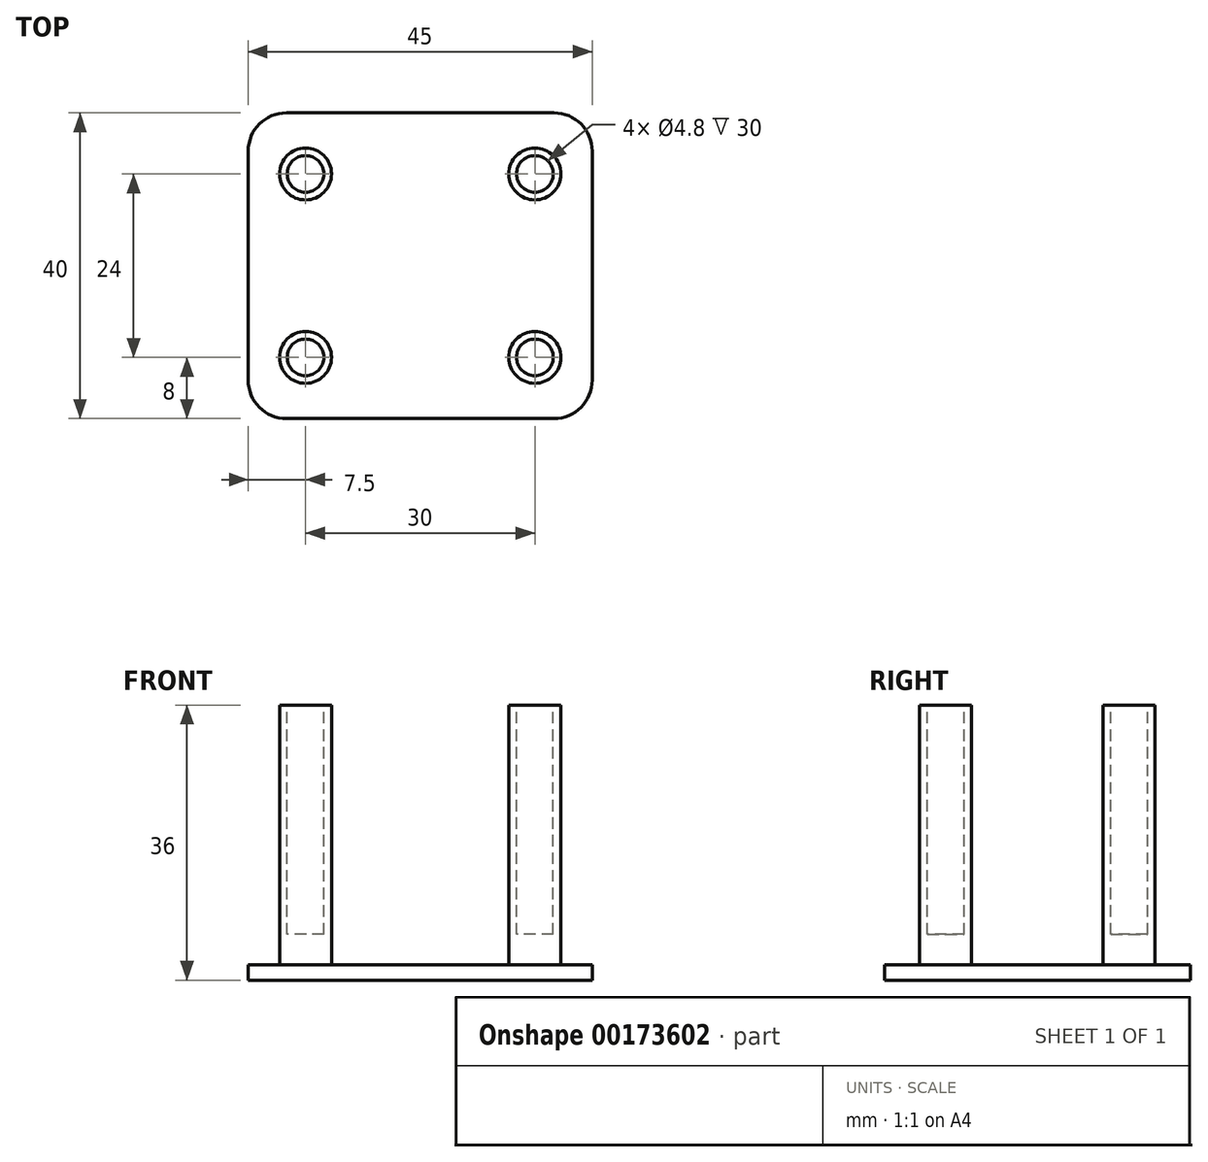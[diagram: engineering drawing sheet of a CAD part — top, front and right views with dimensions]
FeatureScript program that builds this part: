
annotation { "Feature Type Name" : "Feature", "Feature Type Description" : "" }
export const myFeature = defineFeature(function(context is Context, id is Id, definition is map)
    precondition{}
    {
        {
            var Q0;
            Q0=qCreatedBy(makeId("Top.planeOp"),FACE);
            var sketch = newSketch(context, id + "F0", { "sketchPlane" : qUnion([Q0])});
            skLineSegment(sketch, "E0.bottom", {"start": v(22.5, -20) * mm, "end": v(-22.5, -20) * mm});
            skLineSegment(sketch, "E0.top", {"start": v(22.5, 20) * mm, "end": v(-22.5, 20) * mm});
            skLineSegment(sketch, "E0.left", {"start": v(22.5, -20) * mm, "end": v(22.5, 20) * mm});
            skLineSegment(sketch, "E0.right", {"start": v(-22.5, -20) * mm, "end": v(-22.5, 20) * mm});
            skPoint(sketch, "E0.middle", {"position": v(0, 0) * mm});
            skSolve(sketch);
        }
        {
            var Q0;
            Q0 = qSketchRegion(id + "F0", true);
            extrude(context, id + "F1", {"entities" : qUnion([Q0]), "depth" : 2 * mm});
        }
        {
            var Q0;
            Q0=makeQuery(id+"F1.opExtrude","CAP_FACE",FACE,{"disambiguationData":[OSD([sQuery(id+"F0.wireOp",EDGE,"E0.bottom"),sQuery(id+"F0.wireOp",EDGE,"E0.top"),sQuery(id+"F0.wireOp",EDGE,"E0.left"),sQuery(id+"F0.wireOp",EDGE,"E0.right")])],"isStart":false});
            var sketch = newSketch(context, id + "F2", { "sketchPlane" : qUnion([Q0])});
            skLineSegment(sketch, "E1.bottom", {"start": v(15, 12) * mm, "end": v(-15, 12) * mm, "construction": true});
            skLineSegment(sketch, "E1.top", {"start": v(15, -12) * mm, "end": v(-15, -12) * mm, "construction": true});
            skLineSegment(sketch, "E1.left", {"start": v(15, 12) * mm, "end": v(15, -12) * mm, "construction": true});
            skLineSegment(sketch, "E1.right", {"start": v(-15, 12) * mm, "end": v(-15, -12) * mm, "construction": true});
            skPoint(sketch, "E1.middle", {"position": v(0, 0) * mm});
            skCircle(sketch, "E2", {"center": v(-15, 12) * mm, "radius": 3.4 * mm});
            skCircle(sketch, "E3", {"center": v(15, 12) * mm, "radius": 3.4 * mm});
            skCircle(sketch, "E4", {"center": v(15, -12) * mm, "radius": 3.4 * mm});
            skCircle(sketch, "E5", {"center": v(-15, -12) * mm, "radius": 3.4 * mm});
            skSolve(sketch);
        }
        {
            var Q0;
            Q0 = qSketchRegion(id + "F2", true);
            extrude(context, id + "F3", {"entities" : qUnion([Q0]), "operationType" : NewBodyOperationType.ADD, "depth" : 34 * mm});
        }
        {
            var Q0;
            Q0=makeQuery(id+"F3.opExtrude","CAP_FACE",FACE,{"disambiguationData":[OSD([sQuery(id+"F2.wireOp",EDGE,"E2")])],"isStart":false});
            var sketch = newSketch(context, id + "F4", { "sketchPlane" : qUnion([Q0])});
            skCircle(sketch, "E6.0", {"center": v(-15, 12) * mm, "radius": 3.4 * mm, "construction": true});
            skCircle(sketch, "E7.0", {"center": v(15, 12) * mm, "radius": 3.4 * mm, "construction": true});
            skCircle(sketch, "E8.0", {"center": v(15, -12) * mm, "radius": 3.4 * mm, "construction": true});
            skCircle(sketch, "E9.0", {"center": v(-15, -12) * mm, "radius": 3.4 * mm, "construction": true});
            skCircle(sketch, "E10", {"center": v(-15, 12) * mm, "radius": 2.4 * mm});
            skCircle(sketch, "E11", {"center": v(15, 12) * mm, "radius": 2.4 * mm});
            skCircle(sketch, "E12", {"center": v(15, -12) * mm, "radius": 2.4 * mm});
            skCircle(sketch, "E13", {"center": v(-15, -12) * mm, "radius": 2.4 * mm});
            skSolve(sketch);
        }
        {
            var Q0;
            Q0 = qSketchRegion(id + "F4", true);
            extrude(context, id + "F5", {"entities" : qUnion([Q0]), "operationType" : NewBodyOperationType.REMOVE, "oppositeDirection" : true, "depth" : 30 * mm});
        }
        {
            var Q0;
            Q0=makeQuery(id+"F1.opExtrude","SWEPT_EDGE",EDGE,{"disambiguationData":[OSD([sQuery(id+"F0.wireOp",EDGE,"E0.bottom"),sQuery(id+"F0.wireOp",EDGE,"E0.right")])]});
            var Q1;
            Q1=makeQuery(id+"F1.opExtrude","SWEPT_EDGE",EDGE,{"disambiguationData":[OSD([sQuery(id+"F0.wireOp",EDGE,"E0.bottom"),sQuery(id+"F0.wireOp",EDGE,"E0.left")])]});
            var Q2;
            Q2=makeQuery(id+"F1.opExtrude","SWEPT_EDGE",EDGE,{"disambiguationData":[OSD([sQuery(id+"F0.wireOp",EDGE,"E0.top"),sQuery(id+"F0.wireOp",EDGE,"E0.left")])]});
            var Q3;
            Q3=makeQuery(id+"F1.opExtrude","SWEPT_EDGE",EDGE,{"disambiguationData":[OSD([sQuery(id+"F0.wireOp",EDGE,"E0.top"),sQuery(id+"F0.wireOp",EDGE,"E0.right")])]});
            fillet(context, id + "F6", {"entities" : qUnion([Q0, Q1, Q2, Q3]), "radius" : 5 * mm, "tangentPropagation" : true, "allowEdgeOverflow" : false});
        }
    });
